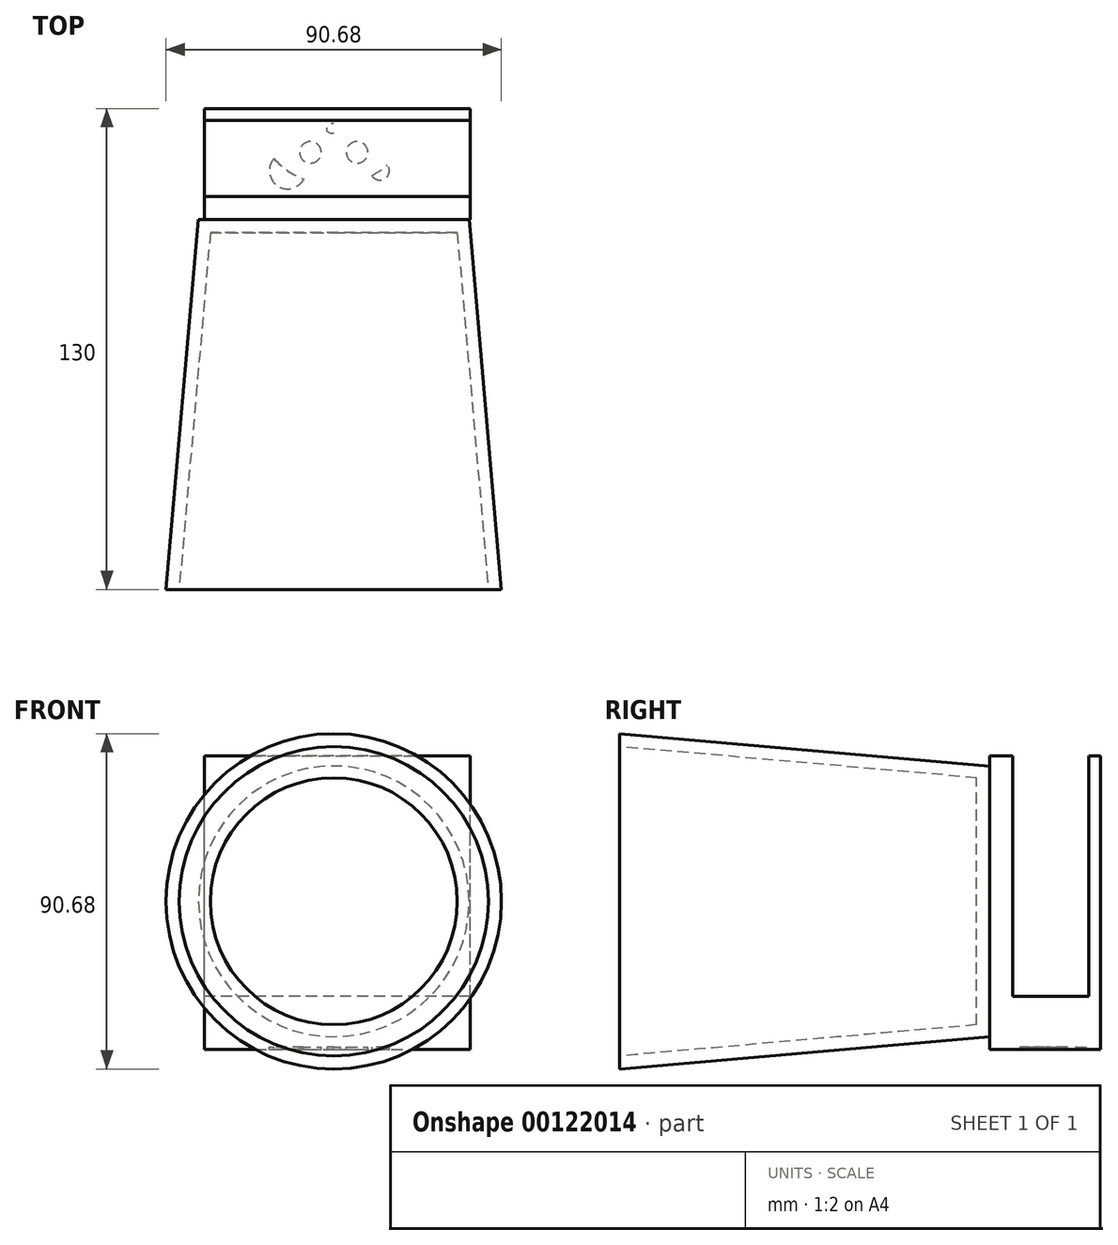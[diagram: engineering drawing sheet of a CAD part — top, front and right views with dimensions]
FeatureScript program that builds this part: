
annotation { "Feature Type Name" : "Feature", "Feature Type Description" : "" }
export const myFeature = defineFeature(function(context is Context, id is Id, definition is map)
    precondition{}
    {
        {
            var Q0;
            Q0=qCreatedBy(makeId("Front.planeOp"),FACE);
            var sketch = newSketch(context, id + "F0", { "sketchPlane" : qUnion([Q0])});
            skLineSegment(sketch, "E0.bottom", {"start": v(-35, -39.38) * mm, "end": v(36.91, -39.38) * mm});
            skLineSegment(sketch, "E0.top", {"start": v(-35, 39.35) * mm, "end": v(36.91, 39.35) * mm});
            skLineSegment(sketch, "E0.left", {"start": v(-35, -39.38) * mm, "end": v(-35, 39.35) * mm});
            skLineSegment(sketch, "E0.right", {"start": v(36.91, -39.38) * mm, "end": v(36.91, 39.35) * mm});
            skSolve(sketch);
        }
        {
            var Q0;
            Q0=makeQuery(id+"F0.imprint","IMPRINT",FACE,{"disambiguationData":[TD([[makeQuery(id+"F0.imprint","IMPRINT",EDGE,{"derivedFrom":sQuery(id+"F0.wireOp",EDGE,"ixIKmrZH-6J3O-kXYH-UssA-IoUKFZQv8jiG")}),1.0]])]});
            var Q1;
            Q1=makeQuery(id+"F0.imprint","IMPRINT",FACE,{"disambiguationData":[TD([[makeQuery(id+"F0.imprint","IMPRINT",EDGE,{"derivedFrom":sQuery(id+"F0.wireOp",EDGE,"E0.bottom")}),1.0]])]});
            extrude(context, id + "F1", {"entities" : qUnion([Q0, Q1]), "oppositeDirection" : true, "depth" : 30 * mm});
        }
        {
            var Q0;
            Q0=qCreatedBy(makeId("Front.planeOp"),FACE);
            var sketch = newSketch(context, id + "F2", { "sketchPlane" : qUnion([Q0])});
            skCircle(sketch, "E1", {"center": v(0, 0) * mm, "radius": 36.59 * mm});
            skSolve(sketch);
        }
        {
            var Q0;
            Q0 = qSketchRegion(id + "F2", true);
            extrude(context, id + "F3", {"entities" : qUnion([Q0]), "depth" : 100 * mm, "hasDraft" : true, "draftAngle" : 5 * degree});
        }
        {
            var Q0;
            Q0=makeQuery(id+"F3.opExtrude","CAP_FACE",FACE,{"disambiguationData":[OSD([sQuery(id+"F2.wireOp",EDGE,"E1")])],"isStart":false});
            var Q1;
            Q1=makeQuery(id+"F1.opExtrude","SWEPT_FACE",FACE,{"disambiguationData":[OSD([sQuery(id+"F0.wireOp",EDGE,"ixIKmrZH-6J3O-kXYH-UssA-IoUKFZQv8jiG")])]});
            shell(context, id + "F4", {"entities" : qUnion([Q0, Q1]), "thickness" : 3.5 * mm});
        }
        {
            var Q0;
            Q0=makeQuery(id+"F1.opExtrude","SWEPT_FACE",FACE,{"disambiguationData":[OSD([sQuery(id+"F0.wireOp",EDGE,"E0.top")])]});
            var sketch = newSketch(context, id + "F5", { "sketchPlane" : qUnion([Q0])});
            skLineSegment(sketch, "E2.bottom", {"start": v(36.91, 6.28) * mm, "end": v(-35, 6.28) * mm});
            skLineSegment(sketch, "E2.top", {"start": v(36.91, 26.76) * mm, "end": v(-35, 26.76) * mm});
            skLineSegment(sketch, "E2.left", {"start": v(36.91, 6.28) * mm, "end": v(36.91, 26.76) * mm});
            skLineSegment(sketch, "E2.right", {"start": v(-35, 6.28) * mm, "end": v(-35, 26.76) * mm});
            skSolve(sketch);
        }
        {
            var Q0;
            Q0 = qSketchRegion(id + "F5", true);
            extrude(context, id + "F6", {"entities" : qUnion([Q0]), "operationType" : NewBodyOperationType.REMOVE, "oppositeDirection" : true, "depth" : 65 * mm});
        }
        {
            var Q0;
            Q0=makeQuery(id+"F1.opExtrude","SWEPT_FACE",FACE,{"disambiguationData":[OSD([sQuery(id+"F0.wireOp",EDGE,"E0.bottom")])]});
            var sketch = newSketch(context, id + "F7", { "sketchPlane" : qUnion([Q0])});
            skArc(sketch, "E3", {"start": v(21.31, -30) * mm, "mid": v(15, -15.27) * mm, "end": v(0, -9.67) * mm});
            skArc(sketch, "E4", {"start": v(16.17, -16.47) * mm, "mid": v(15.26, -9.16) * mm, "end": v(8.11, -10.95) * mm});
            skArc(sketch, "E5", {"start": v(14.48, -14.78) * mm, "mid": v(13.91, -11.12) * mm, "end": v(10.3, -11.91) * mm});
            skArc(sketch, "E6.MirrorCS", {"start": v(-21.31, -30) * mm, "mid": v(-15, -15.27) * mm, "end": v(0, -9.67) * mm});
            skArc(sketch, "E7.MirrorCS", {"start": v(-16.17, -16.47) * mm, "mid": v(-15.26, -9.16) * mm, "end": v(-8.11, -10.95) * mm});
            skArc(sketch, "E8.MirrorCS", {"start": v(-14.48, -14.78) * mm, "mid": v(-13.91, -11.12) * mm, "end": v(-10.3, -11.91) * mm});
            skCircle(sketch, "E9", {"center": v(6.32, -18.18) * mm, "radius": 2.92 * mm});
            skFitSpline(sketch, "E10", {"points": [v(0, -23.33) * mm, v(1.8, -24) * mm, v(1.13, -25.76) * mm, v(0, -26.1) * mm], "startDerivative": vector(6.8, 1.87) * mm, "endDerivative": vector(-4.04, 0.02) * mm});
            skFitSpline(sketch, "E11.MirrorCS", {"points": [v(0, -23.33) * mm, v(-1.8, -24) * mm, v(-1.13, -25.76) * mm, v(0, -26.1) * mm], "startDerivative": vector(-6.8, 1.87) * mm, "endDerivative": vector(4.04, 0.02) * mm});
            skCircle(sketch, "E12.MirrorC", {"center": v(-6.32, -18.18) * mm, "radius": 2.92 * mm});
            skSolve(sketch);
        }
        {
            var Q0;
            {var subQ0=sQuery(id+"F7.wireOp",EDGE,"E4");Q0=makeQuery(id+"F7.imprint","IMPRINT",FACE,{"disambiguationData":[TD([[makeQuery(id+"F7.imprint","IMPRINT",EDGE,{"derivedFrom":subQ0}),1.0]])]});}
            var Q1;
            Q1=makeQuery(id+"F7.imprint","IMPRINT",FACE,{"disambiguationData":[TD([[makeQuery(id+"F7.imprint","IMPRINT",EDGE,{"derivedFrom":sQuery(id+"F7.wireOp",EDGE,"E9")}),-1.0]])]});
            var Q2;
            {var subQ0=sQuery(id+"F7.wireOp",EDGE,"E7.MirrorCS");Q2=makeQuery(id+"F7.imprint","IMPRINT",FACE,{"disambiguationData":[TD([[makeQuery(id+"F7.imprint","IMPRINT",EDGE,{"derivedFrom":subQ0}),-1.0]])]});}
            extrude(context, id + "F8", {"entities" : qUnion([Q0, Q1, Q2]), "operationType" : NewBodyOperationType.ADD, "depth" : 0.7 * mm});
        }
    });
